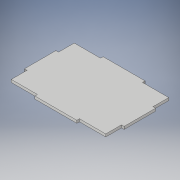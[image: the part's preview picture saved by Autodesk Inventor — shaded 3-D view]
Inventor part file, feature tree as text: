
AUTODESK INVENTOR PART (.ipt)
format: ipt  version: 2019 (Build 230136000, 136)  size: 126,976 bytes
history: native  units: in
note: dims shown in document units (in); Inventor stores cm internally (conversion verified against a paired STEP export)
features: extrude x2, sketch x2
ambient origin geometry x8: Origin, YZ Plane, XZ Plane, XY Plane, X Axis, Y Axis, Z Axis, Center Point
bodies: Solid1 (feature_tree)
feature tree (4):
  extrude  "Extrusion1"  Depth=3.0in
  extrude  "Extrusion2"  Depth=2.0in
  sketch  "Sketch1"  dims[d0=4.5in d1=3.0in]
  sketch  "Sketch2"  dims[d2=0.125in d3=0.0in d4=2.0in d5=0.125in d6=0.0in d7=1.25in d8=1.5in d9=0.125in d10=0.75in d11=0.125in d12=0.0in]
